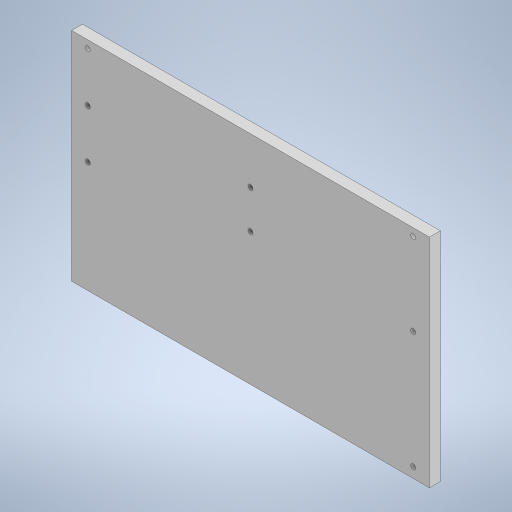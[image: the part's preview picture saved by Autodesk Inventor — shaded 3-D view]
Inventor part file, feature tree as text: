
AUTODESK INVENTOR PART (.ipt)
format: ipt  version: 2023 (Build 270158000, 158)  size: 221,696 bytes
history: native  units: mm
features: extrude x2, sketch x2
ambient origin geometry x8: Origin, YZ Plane, XZ Plane, XY Plane, X Axis, Y Axis, Z Axis, Center Point
bodies: Solide1 (feature_tree)
feature tree (4):
  extrude  "Extrusion1"  Depth=220.0mm
  extrude  "Extrusion2"  Depth=133.5mm
  sketch  "Esquisse1"
  sketch  "Esquisse2"
